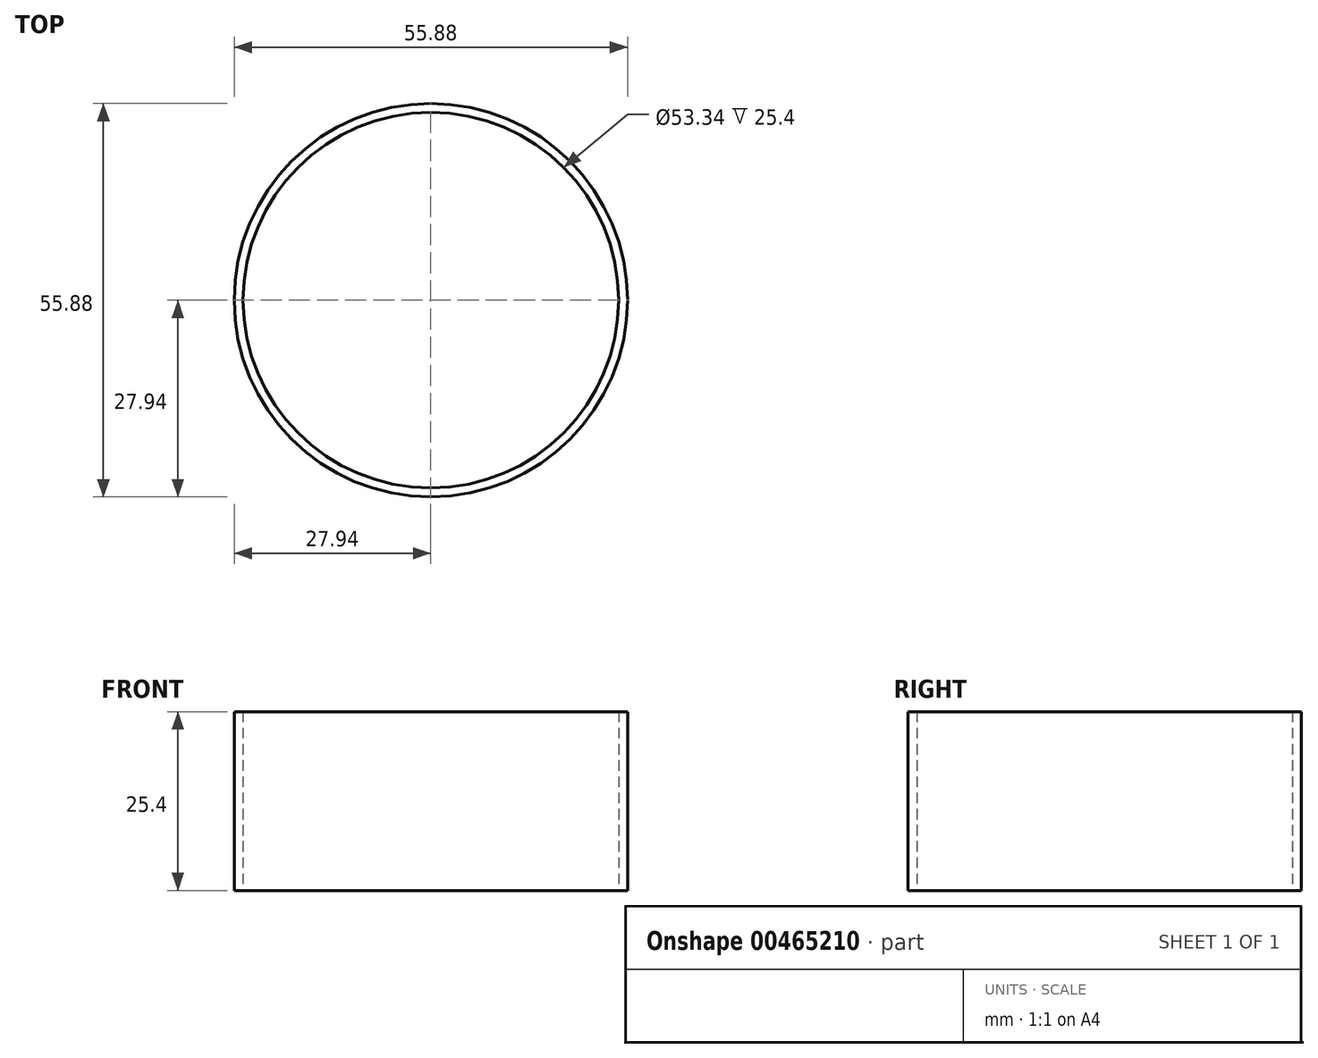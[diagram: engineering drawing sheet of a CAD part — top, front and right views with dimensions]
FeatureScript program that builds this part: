
annotation { "Feature Type Name" : "Feature", "Feature Type Description" : "" }
export const myFeature = defineFeature(function(context is Context, id is Id, definition is map)
    precondition{}
    {
        {
            var Q0;
            Q0=qCreatedBy(makeId("Top.planeOp"),FACE);
            var sketch = newSketch(context, id + "F0", { "sketchPlane" : qUnion([Q0])});
            skCircle(sketch, "E0", {"center": v(0, 0) * mm, "radius": 26.67 * mm});
            skCircle(sketch, "E1", {"center": v(0, 0) * mm, "radius": 27.94 * mm});
            skSolve(sketch);
        }
        {
            var Q0;
            Q0=makeQuery(id+"F0.imprint","IMPRINT",FACE,{"disambiguationData":[TD([[makeQuery(id+"F0.imprint","IMPRINT",EDGE,{"derivedFrom":sQuery(id+"F0.wireOp",EDGE,"E0")}),-1.0]])]});
            extrude(context, id + "F1", {"entities" : qUnion([Q0]), "depth" : 25.4 * mm});
        }
    });
